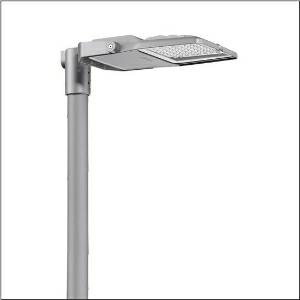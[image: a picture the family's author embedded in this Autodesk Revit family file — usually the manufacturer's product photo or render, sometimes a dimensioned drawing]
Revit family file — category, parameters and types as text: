
# Revit family: floodlight_fl_21_mini___pl52_5xa7776b4d3a_8fbb
name_source: partatom
category: Lighting Fixtures
units: mm (PartAtom-declared; Revit-internal decimal feet)

## family parameters
Cut with Voids When Loaded = No
Host = Face
Light Source = No
Part Type = Normal
Room Calculation Point = No
Round Connector Dimension = Use Diameter
Shared = No

## types (1)
- --- (1 x LED, 6480 lm, 45.7 W, 4000K)
    Apparent Load = 46 VA
    CIE Flux Codes = 26 60 98 100 100
    Color Rendering = 70
    Color Temperature = 4000K
    Default Elevation = 1800 mm
    Description = Floodlight FL 21 mini, floodlight, primary light control with lens, of PMMA, primary optical cover: protective disc, of toughened safety glass, transparent, light distribution: PL52, light emission: direct distribution, installation type: surface-mounted, LED, High Power LED, rated luminous flux: 6.480lm, luminous efficacy: 142lm/W, light colour: 740, colour temperature: 4000K, control gear: D4iSmart Interface (Zhaga), control: overheat protection, constant luminous flux control, time-dependent luminous flux control, flexible luminous flux parameterisation, pre-setting: logarithmic dimming characteristic, with terminal, 6-pole, mains connection: 220..240V, AC, 50/60Hz, start of lifetime: 46W, end of service life: 48W, reduction: 22W, mast bracket, of diecast aluminium, powder-coated, Siteco® metallic grey (DB 702S), corrosivity category C5 mid according to DIN EN ISO 12944, suitable for swimming pools, chlorine-resistant, sealing non-destructively replaceable, mast bracket, of steel, galvanised, powder-coated, Siteco® metallic grey (DB 702S), Smart Interface below and above, protection rating (complete): IP66, insulation class (complete): insulation class II (safety insulation), certification: CE, ENEC, VDE, protection symbol: D, impact resistance: IK08, permissible operating ambient temperature: -40..+40°C, permissible operating ambient temperature for outdoor applications: -40..+50°C, standard: DIN EN 12944, LABS conformity tested according to VDMA 24364:2018-05, packaging unit: 1 piece

Light Distribution: PL52
    Height = 70 mm
    Lamp = 1 x LED
    Lamp Light Flux = 6480 lm
    Lamp Power = 45.7 W
    Lamp count = 1
    Length = 485 mm
    Luminous efficacy = 142 lm/W
    Manufacturer = Siteco
    ModVariant = No
    Model = 5XA7776B4D3A
    Number of Poles = 1
    OnlyDefault = Yes
    Power Factor = 1
    Product Name = Floodlight FL 21 mini | PL52
    Product group = floodlight | pylon annexe
    ProductGroupID = 6200
    Protection Class = Protection class II
    Protection Degree = IP 66
    RLX_Detail_Level = 1
    RLX_Emergency_Light_Flux = 0 lm
    RLX_Emergency_Type = 0
    RLX_Emergency_Type_DB = No
    RlxData = <blob elided: 101209 chars, md5=f6807ed6>
    Socket = socket
    Standby Power = 0 W
    System Light Flux = 6480 lm
    System Power = 46 W
    Type Comments = factory setting: luminous flux: 100 % | dim-lin: 254 | 463 mA
    Type Image = l_1007125.jpg
    URL = http://relux.com
    VarID = @adj_095440
    Voltage = 0 V
    Weight = 0.00 kg
    Width = 337 mm

## geometry (parser evidence)
native form markers: Blend x4, Sweep x12
no freeform markers — native parametric forms only
